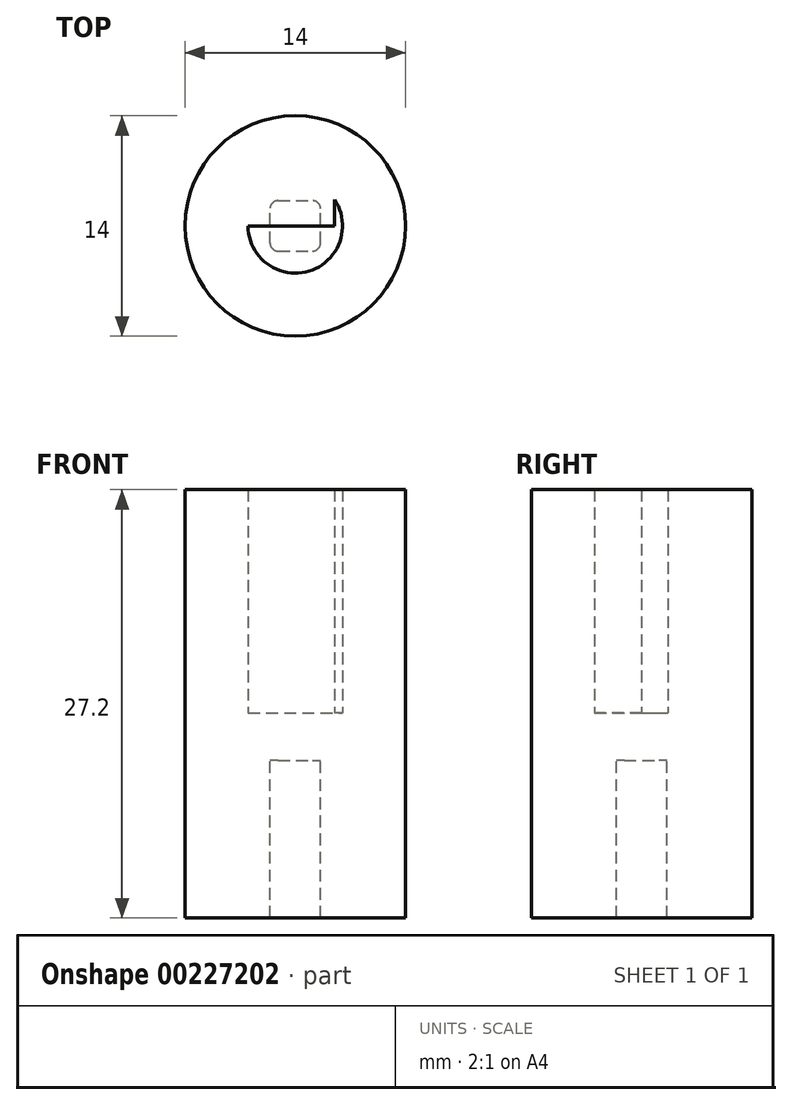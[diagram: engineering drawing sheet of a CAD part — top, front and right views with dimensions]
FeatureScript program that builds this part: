
annotation { "Feature Type Name" : "Feature", "Feature Type Description" : "" }
export const myFeature = defineFeature(function(context is Context, id is Id, definition is map)
    precondition{}
    {
        {
            var Q0;
            Q0=qCreatedBy(makeId("Top.planeOp"),FACE);
            var sketch = newSketch(context, id + "F0", { "sketchPlane" : qUnion([Q0])});
            skCircle(sketch, "E0", {"center": v(0, 0) * mm, "radius": 3 * mm});
            skLineSegment(sketch, "E1", {"start": v(-3, 0) * mm, "end": v(2.5, 0) * mm});
            skLineSegment(sketch, "E2", {"start": v(2.5, -1.66) * mm, "end": v(2.5, 1.66) * mm});
            skCircle(sketch, "E3", {"center": v(0, 0) * mm, "radius": 7 * mm});
            skSolve(sketch);
        }
        {
            var Q0;
            Q0=makeQuery(id+"F0.imprint","IMPRINT",FACE,{"disambiguationData":[TD([[makeQuery(id+"F0.imprint","IMPRINT",EDGE,{"derivedFrom":sQuery(id+"F0.wireOp",EDGE,"E3")}),1.0]])]});
            var Q1;
            {var subQ0=sQuery(id+"F0.wireOp",EDGE,"E2");var subQ1=sQuery(id+"F0.wireOp",EDGE,"E0");var subQ2=makeQuery(id+"F0.imprint","INTERSECT",VERTEX,{"disambiguationData":[OD(0.0)],"derivedFrom":[subQ1,subQ0]});Q1=makeQuery(id+"F0.imprint","IMPRINT",FACE,{"disambiguationData":[TD([[makeQuery(id+"F0.imprint","IMPRINT",EDGE,{"disambiguationData":[TD([[subQ2,-1.0]])],"derivedFrom":subQ1}),1.0]])]});}
            extrude(context, id + "F1", {"entities" : qUnion([Q0, Q1]), "depth" : 14.2 * mm});
        }
        {
            var Q0;
            Q0=makeQuery(id+"F1.opExtrude","CAP_FACE",FACE,{"disambiguationData":[OSD([sQuery(id+"F0.wireOp",EDGE,"E0"),sQuery(id+"F0.wireOp",EDGE,"E2"),sQuery(id+"F0.wireOp",EDGE,"E3")])],"isStart":true});
            var sketch = newSketch(context, id + "F2", { "sketchPlane" : qUnion([Q0])});
            skCircle(sketch, "E4", {"center": v(0, 0) * mm, "radius": 5 * mm});
            skSolve(sketch);
        }
        {
            var Q0;
            Q0=makeQuery(id+"F2.imprint","IMPRINT",FACE,{"disambiguationData":[TD([[makeQuery(id+"F2.imprint","IMPRINT",EDGE,{"derivedFrom":sQuery(id+"F2.wireOp",EDGE,"E4")}),-1.0]])]});
            var Q1;
            Q1=makeQuery(id+"F2.imprint","IMPRINT",FACE,{"disambiguationData":[TD([[makeQuery(id+"F2.imprint","IMPRINT",EDGE,{"derivedFrom":sQuery(id+"F2.wireOp",EDGE,"E4")}),1.0]])]});
            var Q2;
            Q2=makeQuery(id+"F2.imprint","IMPRINT",FACE,{"disambiguationData":[TD([[makeQuery(id+"F2.imprint","IMPRINT",EDGE,{"derivedFrom":makeQuery(id+"F1.opExtrude","CAP_EDGE",EDGE,{"disambiguationData":[OSD([sQuery(id+"F0.wireOp",EDGE,"E0")])],"isStart":true})}),-1.0]])]});
            extrude(context, id + "F3", {"entities" : qUnion([Q0, Q1, Q2]), "operationType" : NewBodyOperationType.ADD, "depth" : 3 * mm});
        }
        {
            var Q0;
            Q0=makeQuery(id+"F3.opExtrude","CAP_FACE",FACE,{"disambiguationData":[OSD([sQuery(id+"F0.wireOp",EDGE,"E3")])],"isStart":false});
            var sketch = newSketch(context, id + "F4", { "sketchPlane" : qUnion([Q0])});
            skLineSegment(sketch, "E5.bottom", {"start": v(-1.6, 1.6) * mm, "end": v(1.6, 1.6) * mm});
            skLineSegment(sketch, "E5.top", {"start": v(-1.6, -1.6) * mm, "end": v(1.6, -1.6) * mm});
            skLineSegment(sketch, "E5.left", {"start": v(-1.6, 1.6) * mm, "end": v(-1.6, -1.6) * mm});
            skLineSegment(sketch, "E5.right", {"start": v(1.6, 1.6) * mm, "end": v(1.6, -1.6) * mm});
            skPoint(sketch, "E5.middle", {"position": v(0, 0) * mm});
            skCircle(sketch, "E6", {"center": v(0, 0) * mm, "radius": 5 * mm});
            skSolve(sketch);
        }
        {
            var Q0;
            Q0=makeQuery(id+"F4.imprint","IMPRINT",FACE,{"disambiguationData":[TD([[makeQuery(id+"F4.imprint","IMPRINT",EDGE,{"derivedFrom":sQuery(id+"F4.wireOp",EDGE,"E5.bottom")}),1.0]])]});
            var Q1;
            Q1=makeQuery(id+"F4.imprint","IMPRINT",FACE,{"disambiguationData":[TD([[makeQuery(id+"F4.imprint","IMPRINT",EDGE,{"derivedFrom":sQuery(id+"F4.wireOp",EDGE,"E6")}),-1.0]])]});
            extrude(context, id + "F5", {"entities" : qUnion([Q0, Q1]), "operationType" : NewBodyOperationType.ADD, "depth" : 10 * mm});
        }
        {
            var Q0;
            Q0=makeQuery(id+"F5.opExtrude","SWEPT_EDGE",EDGE,{"disambiguationData":[OSD([sQuery(id+"F4.wireOp",EDGE,"E5.bottom"),sQuery(id+"F4.wireOp",EDGE,"E5.left")])]});
            var Q1;
            Q1=makeQuery(id+"F5.opExtrude","SWEPT_EDGE",EDGE,{"disambiguationData":[OSD([sQuery(id+"F4.wireOp",EDGE,"E5.top"),sQuery(id+"F4.wireOp",EDGE,"E5.left")])]});
            var Q2;
            Q2=makeQuery(id+"F5.opExtrude","SWEPT_EDGE",EDGE,{"disambiguationData":[OSD([sQuery(id+"F4.wireOp",EDGE,"E5.bottom"),sQuery(id+"F4.wireOp",EDGE,"E5.right")])]});
            var Q3;
            Q3=makeQuery(id+"F5.opExtrude","SWEPT_EDGE",EDGE,{"disambiguationData":[OSD([sQuery(id+"F4.wireOp",EDGE,"E5.top"),sQuery(id+"F4.wireOp",EDGE,"E5.right")])]});
            fillet(context, id + "F6", {"entities" : qUnion([Q0, Q1, Q2, Q3]), "radius" : 0.5 * mm, "tangentPropagation" : true, "allowEdgeOverflow" : false});
        }
    });
